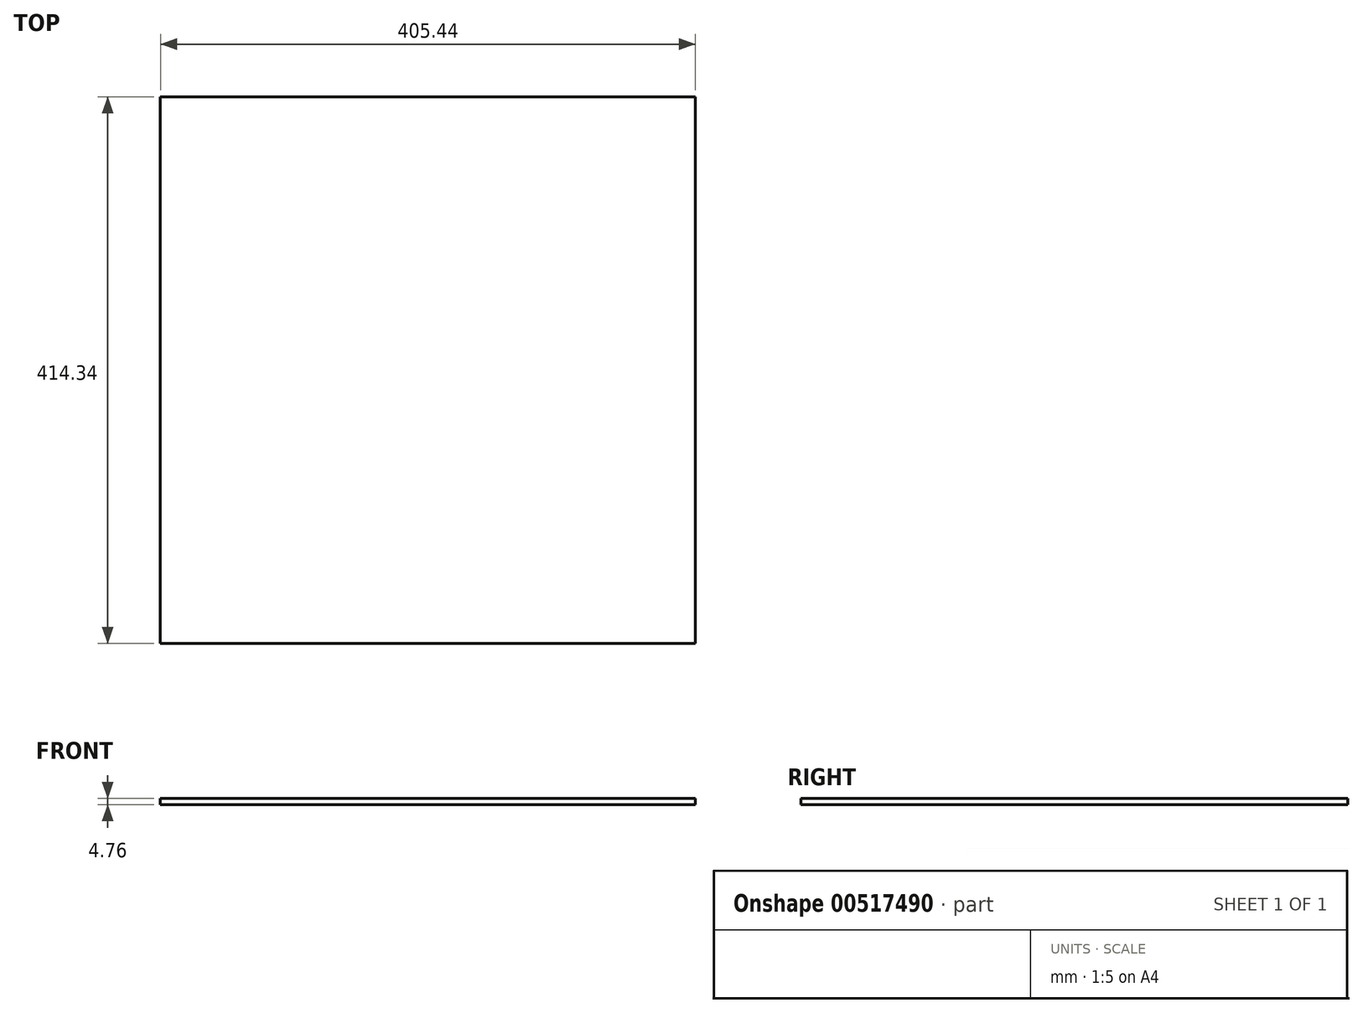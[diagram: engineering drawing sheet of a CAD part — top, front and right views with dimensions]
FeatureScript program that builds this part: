
annotation { "Feature Type Name" : "Feature", "Feature Type Description" : "" }
export const myFeature = defineFeature(function(context is Context, id is Id, definition is map)
    precondition{}
    {
        {
            var Q0;
            Q0=qCreatedBy(makeId("Top.planeOp"),FACE);
            var sketch = newSketch(context, id + "F0", { "sketchPlane" : qUnion([Q0])});
            skLineSegment(sketch, "E0.bottom", {"start": v(-202.72, 207.17) * mm, "end": v(202.72, 207.17) * mm});
            skLineSegment(sketch, "E0.top", {"start": v(-202.72, -207.17) * mm, "end": v(202.72, -207.17) * mm});
            skLineSegment(sketch, "E0.left", {"start": v(-202.72, 207.17) * mm, "end": v(-202.72, -207.17) * mm});
            skLineSegment(sketch, "E0.right", {"start": v(202.72, 207.17) * mm, "end": v(202.72, -207.17) * mm});
            skPoint(sketch, "E0.middle", {"position": v(0, 0) * mm});
            skSolve(sketch);
        }
        {
            var Q0;
            Q0 = qSketchRegion(id + "F0", true);
            extrude(context, id + "F1", {"entities" : qUnion([Q0]), "depth" : 4.76 * mm, "offsetDistance" : 25.4 * mm});
        }
    });
